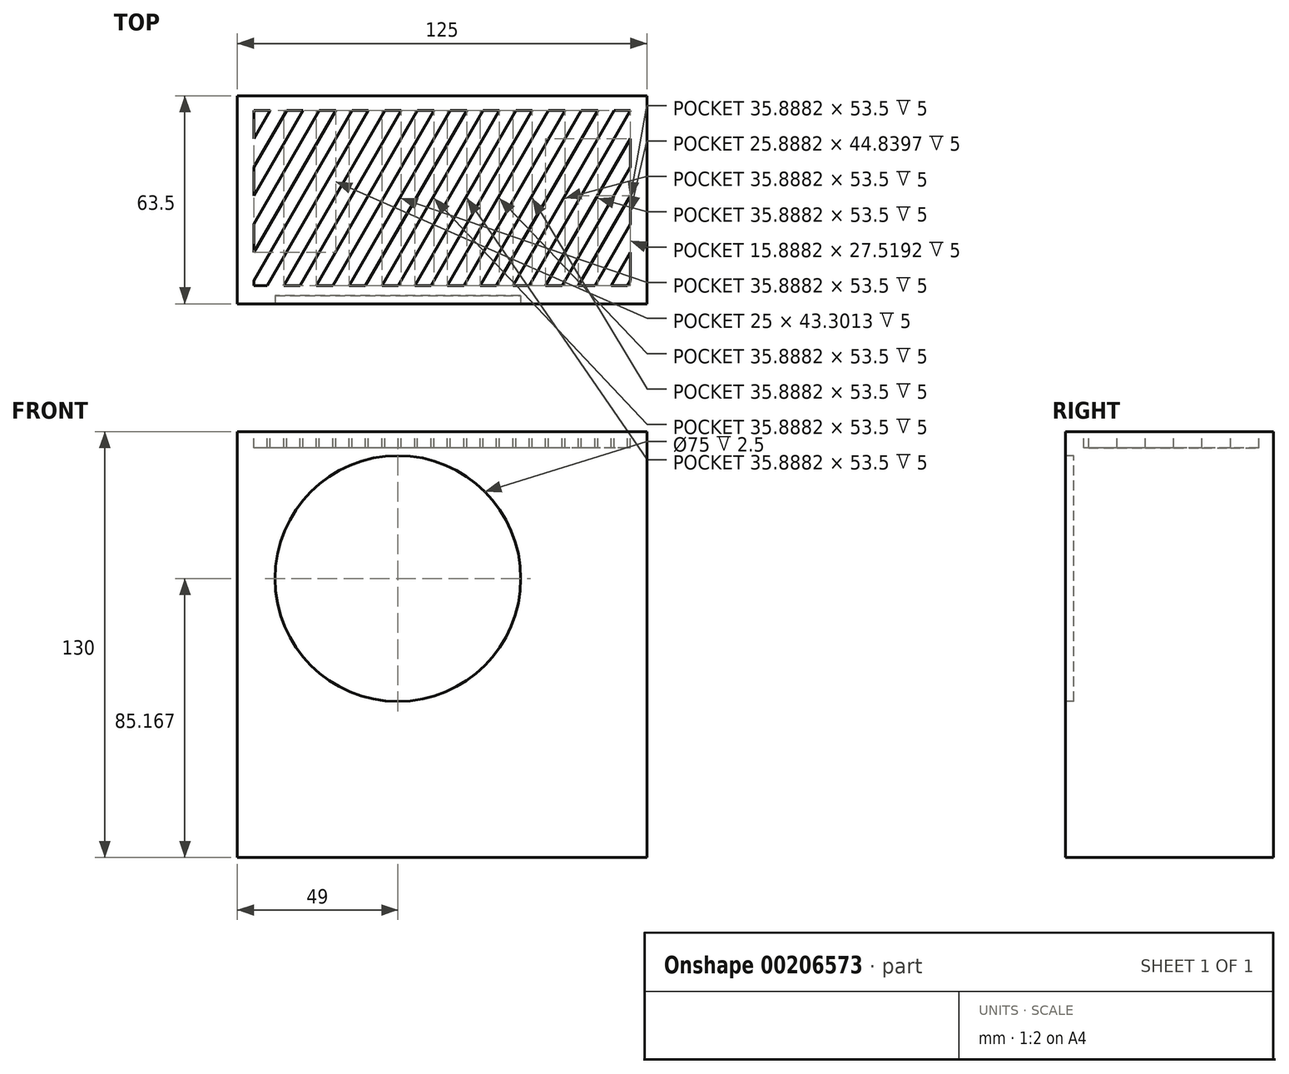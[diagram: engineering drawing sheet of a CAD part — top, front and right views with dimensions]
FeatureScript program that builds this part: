
annotation { "Feature Type Name" : "Feature", "Feature Type Description" : "" }
export const myFeature = defineFeature(function(context is Context, id is Id, definition is map)
    precondition{}
    {
        {
            var Q0;
            Q0=qCreatedBy(makeId("Front.planeOp"),FACE);
            var sketch = newSketch(context, id + "F0", { "sketchPlane" : qUnion([Q0])});
            skLineSegment(sketch, "E0.bottom", {"start": v(-62.5, 67.5) * mm, "end": v(62.5, 67.5) * mm});
            skLineSegment(sketch, "E0.top", {"start": v(-62.5, -32.5) * mm, "end": v(62.5, -32.5) * mm});
            skLineSegment(sketch, "E0.left", {"start": v(-62.5, 67.5) * mm, "end": v(-62.5, -32.5) * mm});
            skLineSegment(sketch, "E0.right", {"start": v(62.5, 67.5) * mm, "end": v(62.5, -32.5) * mm});
            skLineSegment(sketch, "E1.top", {"start": v(-62.5, -62.5) * mm, "end": v(62.5, -62.5) * mm});
            skLineSegment(sketch, "E1.left", {"start": v(-62.5, -32.5) * mm, "end": v(-62.5, -62.5) * mm});
            skLineSegment(sketch, "E1.right", {"start": v(62.5, -32.5) * mm, "end": v(62.5, -62.5) * mm});
            skSolve(sketch);
        }
        {
            var Q0;
            Q0=qCreatedBy(makeId("Front.planeOp"),FACE);
            var sketch = newSketch(context, id + "F1", { "sketchPlane" : qUnion([Q0])});
            skLineSegment(sketch, "E2.bottom", {"start": v(-53.5, 62.67) * mm, "end": v(26.5, 62.67) * mm});
            skLineSegment(sketch, "E2.top", {"start": v(-53.5, -17.33) * mm, "end": v(26.5, -17.33) * mm});
            skLineSegment(sketch, "E2.left", {"start": v(-53.5, 62.67) * mm, "end": v(-53.5, -17.33) * mm});
            skLineSegment(sketch, "E2.right", {"start": v(26.5, 62.67) * mm, "end": v(26.5, -17.33) * mm});
            skPoint(sketch, "E3", {"position": v(-13.5, 22.67) * mm});
            skCircle(sketch, "E4", {"center": v(-13.5, 22.67) * mm, "radius": 37.5 * mm});
            skSolve(sketch);
        }
        {
            var Q0;
            Q0=makeQuery(id+"F0.imprint","IMPRINT",FACE,{"disambiguationData":[TD([[makeQuery(id+"F0.imprint","IMPRINT",EDGE,{"derivedFrom":sQuery(id+"F0.wireOp",EDGE,"E0.bottom")}),-1.0]])]});
            extrude(context, id + "F2", {"entities" : qUnion([Q0]), "oppositeDirection" : true, "depth" : 63.5 * mm});
        }
        {
            var Q0;
            Q0=makeQuery(id+"F0.imprint","IMPRINT",FACE,{"disambiguationData":[TD([[makeQuery(id+"F0.imprint","IMPRINT",EDGE,{"derivedFrom":sQuery(id+"F0.wireOp",EDGE,"E0.top")}),-1.0]])]});
            extrude(context, id + "F3", {"entities" : qUnion([Q0]), "operationType" : NewBodyOperationType.ADD, "oppositeDirection" : true, "depth" : 63.5 * mm});
        }
        {
            var Q0;
            Q0=makeQuery(id+"F1.imprint","IMPRINT",FACE,{"disambiguationData":[TD([[makeQuery(id+"F1.imprint","IMPRINT",EDGE,{"derivedFrom":sQuery(id+"F1.wireOp",EDGE,"E4")}),1.0]])]});
            extrude(context, id + "F4", {"entities" : qUnion([Q0]), "operationType" : NewBodyOperationType.REMOVE, "endBound" : BoundingType.SYMMETRIC, "oppositeDirection" : true, "depth" : 5 * mm});
        }
        {
            var Q0;
            Q0=makeQuery(id+"F2.opExtrude","SWEPT_FACE",FACE,{"disambiguationData":[OSD([sQuery(id+"F0.wireOp",EDGE,"E0.bottom")])]});
            var sketch = newSketch(context, id + "F5", { "sketchPlane" : qUnion([Q0])});
            skLineSegment(sketch, "E5.bottom", {"start": v(57.5, 5.5) * mm, "end": v(-57.5, 5.5) * mm});
            skLineSegment(sketch, "E5.top", {"start": v(57.5, 59) * mm, "end": v(-57.5, 59) * mm});
            skLineSegment(sketch, "E5.left", {"start": v(57.5, 5.5) * mm, "end": v(57.5, 59) * mm});
            skLineSegment(sketch, "E5.right", {"start": v(-57.5, 5.5) * mm, "end": v(-57.5, 59) * mm});
            skPoint(sketch, "E5.middle", {"position": v(0, 32.25) * mm});
            skLineSegment(sketch, "E6", {"start": v(-57.5, 59) * mm, "end": v(-88.39, 5.5) * mm});
            skPoint(sketch, "E7", {"position": v(-72.94, 32.25) * mm});
            skLineSegment(sketch, "E8.1.0.0", {"start": v(-52.5, 59) * mm, "end": v(-83.39, 5.5) * mm});
            skLineSegment(sketch, "E8.2.0.0", {"start": v(-47.5, 59) * mm, "end": v(-78.39, 5.5) * mm});
            skLineSegment(sketch, "E8.3.0.0", {"start": v(-42.5, 59) * mm, "end": v(-73.39, 5.5) * mm});
            skLineSegment(sketch, "E8.4.0.0", {"start": v(-37.5, 59) * mm, "end": v(-68.39, 5.5) * mm});
            skLineSegment(sketch, "E8.5.0.0", {"start": v(-32.5, 59) * mm, "end": v(-63.39, 5.5) * mm});
            skLineSegment(sketch, "E8.6.0.0", {"start": v(-27.5, 59) * mm, "end": v(-58.39, 5.5) * mm});
            skLineSegment(sketch, "E8.7.0.0", {"start": v(-22.5, 59) * mm, "end": v(-53.39, 5.5) * mm});
            skLineSegment(sketch, "E8.8.0.0", {"start": v(-17.5, 59) * mm, "end": v(-48.39, 5.5) * mm});
            skLineSegment(sketch, "E8.9.0.0", {"start": v(-12.5, 59) * mm, "end": v(-43.39, 5.5) * mm});
            skLineSegment(sketch, "E8.10.0.0", {"start": v(-7.5, 59) * mm, "end": v(-38.39, 5.5) * mm});
            skLineSegment(sketch, "E8.11.0.0", {"start": v(-2.5, 59) * mm, "end": v(-33.39, 5.5) * mm});
            skLineSegment(sketch, "E8.12.0.0", {"start": v(2.5, 59) * mm, "end": v(-28.39, 5.5) * mm});
            skLineSegment(sketch, "E8.13.0.0", {"start": v(7.5, 59) * mm, "end": v(-23.39, 5.5) * mm});
            skLineSegment(sketch, "E8.14.0.0", {"start": v(12.5, 59) * mm, "end": v(-18.39, 5.5) * mm});
            skLineSegment(sketch, "E8.15.0.0", {"start": v(17.5, 59) * mm, "end": v(-13.39, 5.5) * mm});
            skLineSegment(sketch, "E8.16.0.0", {"start": v(22.5, 59) * mm, "end": v(-8.39, 5.5) * mm});
            skLineSegment(sketch, "E8.17.0.0", {"start": v(27.5, 59) * mm, "end": v(-3.39, 5.5) * mm});
            skLineSegment(sketch, "E8.18.0.0", {"start": v(32.5, 59) * mm, "end": v(1.61, 5.5) * mm});
            skLineSegment(sketch, "E8.19.0.0", {"start": v(37.5, 59) * mm, "end": v(6.61, 5.5) * mm});
            skLineSegment(sketch, "E8.20.0.0", {"start": v(42.5, 59) * mm, "end": v(11.61, 5.5) * mm});
            skLineSegment(sketch, "E8.21.0.0", {"start": v(47.5, 59) * mm, "end": v(16.61, 5.5) * mm});
            skLineSegment(sketch, "E8.22.0.0", {"start": v(52.5, 59) * mm, "end": v(21.61, 5.5) * mm});
            skLineSegment(sketch, "E8.23.0.0", {"start": v(57.5, 59) * mm, "end": v(26.61, 5.5) * mm});
            skLineSegment(sketch, "E8.24.0.0", {"start": v(62.5, 59) * mm, "end": v(31.61, 5.5) * mm});
            skLineSegment(sketch, "E8.25.0.0", {"start": v(67.5, 59) * mm, "end": v(36.61, 5.5) * mm});
            skLineSegment(sketch, "E8.26.0.0", {"start": v(72.5, 59) * mm, "end": v(41.61, 5.5) * mm});
            skLineSegment(sketch, "E8.27.0.0", {"start": v(77.5, 59) * mm, "end": v(46.61, 5.5) * mm});
            skLineSegment(sketch, "E8.28.0.0", {"start": v(82.5, 59) * mm, "end": v(51.61, 5.5) * mm});
            skLineSegment(sketch, "E8.29.0.0", {"start": v(87.5, 59) * mm, "end": v(56.61, 5.5) * mm});
            skLineSegment(sketch, "E8.direction1", {"start": v(-88.39, 5.5) * mm, "end": v(-83.39, 5.5) * mm, "construction": true});
            skSolve(sketch);
        }
        {
            var Q0;
            {var subQ1=sQuery(id+"F5.wireOp",EDGE,"E5.top");var subQ3=sQuery(id+"F5.wireOp",EDGE,"E8.1.0.0");var subQ4=makeQuery(id+"F5.imprint","INTERSECT",VERTEX,{"derivedFrom":[subQ1,subQ3]});Q0=makeQuery(id+"F5.imprint","IMPRINT",FACE,{"disambiguationData":[TD([[makeQuery(id+"F5.imprint","IMPRINT",EDGE,{"disambiguationData":[TD([[subQ4,-1.0]])],"derivedFrom":subQ3}),-1.0]])]});}
            var Q1;
            {var subQ0=sQuery(id+"F5.wireOp",EDGE,"E8.2.0.0");var subQ1=sQuery(id+"F5.wireOp",EDGE,"E5.top");var subQ2=makeQuery(id+"F5.imprint","INTERSECT",VERTEX,{"derivedFrom":[subQ1,subQ0]});Q1=makeQuery(id+"F5.imprint","IMPRINT",FACE,{"disambiguationData":[TD([[makeQuery(id+"F5.imprint","IMPRINT",EDGE,{"disambiguationData":[TD([[subQ2,1.0]])],"derivedFrom":subQ1}),1.0]])]});}
            var Q2;
            {var subQ0=sQuery(id+"F5.wireOp",EDGE,"E8.4.0.0");var subQ1=sQuery(id+"F5.wireOp",EDGE,"E5.top");var subQ2=makeQuery(id+"F5.imprint","INTERSECT",VERTEX,{"derivedFrom":[subQ1,subQ0]});Q2=makeQuery(id+"F5.imprint","IMPRINT",FACE,{"disambiguationData":[TD([[makeQuery(id+"F5.imprint","IMPRINT",EDGE,{"disambiguationData":[TD([[subQ2,1.0]])],"derivedFrom":subQ1}),1.0]])]});}
            var Q3;
            {var subQ7=sQuery(id+"F5.wireOp",EDGE,"E8.7.0.0");Q3=makeQuery(id+"F5.imprint","IMPRINT",FACE,{"disambiguationData":[TD([[makeQuery(id+"F5.imprint","IMPRINT",EDGE,{"derivedFrom":subQ7}),-1.0]])]});}
            var Q4;
            {var subQ0=sQuery(id+"F5.wireOp",EDGE,"E8.8.0.0");Q4=makeQuery(id+"F5.imprint","IMPRINT",FACE,{"disambiguationData":[TD([[makeQuery(id+"F5.imprint","IMPRINT",EDGE,{"derivedFrom":subQ0}),1.0]])]});}
            var Q5;
            {var subQ0=sQuery(id+"F5.wireOp",EDGE,"E8.10.0.0");Q5=makeQuery(id+"F5.imprint","IMPRINT",FACE,{"disambiguationData":[TD([[makeQuery(id+"F5.imprint","IMPRINT",EDGE,{"derivedFrom":subQ0}),1.0]])]});}
            var Q6;
            {var subQ0=sQuery(id+"F5.wireOp",EDGE,"E8.12.0.0");Q6=makeQuery(id+"F5.imprint","IMPRINT",FACE,{"disambiguationData":[TD([[makeQuery(id+"F5.imprint","IMPRINT",EDGE,{"derivedFrom":subQ0}),1.0]])]});}
            var Q7;
            {var subQ0=sQuery(id+"F5.wireOp",EDGE,"E8.14.0.0");Q7=makeQuery(id+"F5.imprint","IMPRINT",FACE,{"disambiguationData":[TD([[makeQuery(id+"F5.imprint","IMPRINT",EDGE,{"derivedFrom":subQ0}),1.0]])]});}
            var Q8;
            {var subQ0=sQuery(id+"F5.wireOp",EDGE,"E8.16.0.0");Q8=makeQuery(id+"F5.imprint","IMPRINT",FACE,{"disambiguationData":[TD([[makeQuery(id+"F5.imprint","IMPRINT",EDGE,{"derivedFrom":subQ0}),1.0]])]});}
            var Q9;
            {var subQ0=sQuery(id+"F5.wireOp",EDGE,"E8.18.0.0");Q9=makeQuery(id+"F5.imprint","IMPRINT",FACE,{"disambiguationData":[TD([[makeQuery(id+"F5.imprint","IMPRINT",EDGE,{"derivedFrom":subQ0}),1.0]])]});}
            var Q10;
            {var subQ0=sQuery(id+"F5.wireOp",EDGE,"E8.20.0.0");Q10=makeQuery(id+"F5.imprint","IMPRINT",FACE,{"disambiguationData":[TD([[makeQuery(id+"F5.imprint","IMPRINT",EDGE,{"derivedFrom":subQ0}),1.0]])]});}
            var Q11;
            {var subQ0=sQuery(id+"F5.wireOp",EDGE,"E8.22.0.0");Q11=makeQuery(id+"F5.imprint","IMPRINT",FACE,{"disambiguationData":[TD([[makeQuery(id+"F5.imprint","IMPRINT",EDGE,{"derivedFrom":subQ0}),1.0]])]});}
            var Q12;
            {var subQ0=sQuery(id+"F5.wireOp",EDGE,"E8.24.0.0");var subQ1=sQuery(id+"F5.wireOp",EDGE,"E5.bottom");var subQ2=makeQuery(id+"F5.imprint","INTERSECT",VERTEX,{"derivedFrom":[subQ1,subQ0]});Q12=makeQuery(id+"F5.imprint","IMPRINT",FACE,{"disambiguationData":[TD([[makeQuery(id+"F5.imprint","IMPRINT",EDGE,{"disambiguationData":[TD([[subQ2,1.0]])],"derivedFrom":subQ1}),-1.0]])]});}
            var Q13;
            {var subQ0=sQuery(id+"F5.wireOp",EDGE,"E8.26.0.0");var subQ1=sQuery(id+"F5.wireOp",EDGE,"E5.bottom");var subQ2=makeQuery(id+"F5.imprint","INTERSECT",VERTEX,{"derivedFrom":[subQ1,subQ0]});Q13=makeQuery(id+"F5.imprint","IMPRINT",FACE,{"disambiguationData":[TD([[makeQuery(id+"F5.imprint","IMPRINT",EDGE,{"disambiguationData":[TD([[subQ2,1.0]])],"derivedFrom":subQ1}),-1.0]])]});}
            var Q14;
            {var subQ0=sQuery(id+"F5.wireOp",EDGE,"E8.28.0.0");var subQ1=sQuery(id+"F5.wireOp",EDGE,"E5.bottom");var subQ2=makeQuery(id+"F5.imprint","INTERSECT",VERTEX,{"derivedFrom":[subQ1,subQ0]});Q14=makeQuery(id+"F5.imprint","IMPRINT",FACE,{"disambiguationData":[TD([[makeQuery(id+"F5.imprint","IMPRINT",EDGE,{"disambiguationData":[TD([[subQ2,1.0]])],"derivedFrom":subQ1}),-1.0]])]});}
            extrude(context, id + "F6", {"entities" : qUnion([Q0, Q1, Q2, Q3, Q4, Q5, Q6, Q7, Q8, Q9, Q10, Q11, Q12, Q13, Q14]), "operationType" : NewBodyOperationType.REMOVE, "oppositeDirection" : true, "depth" : 5 * mm});
        }
    });
